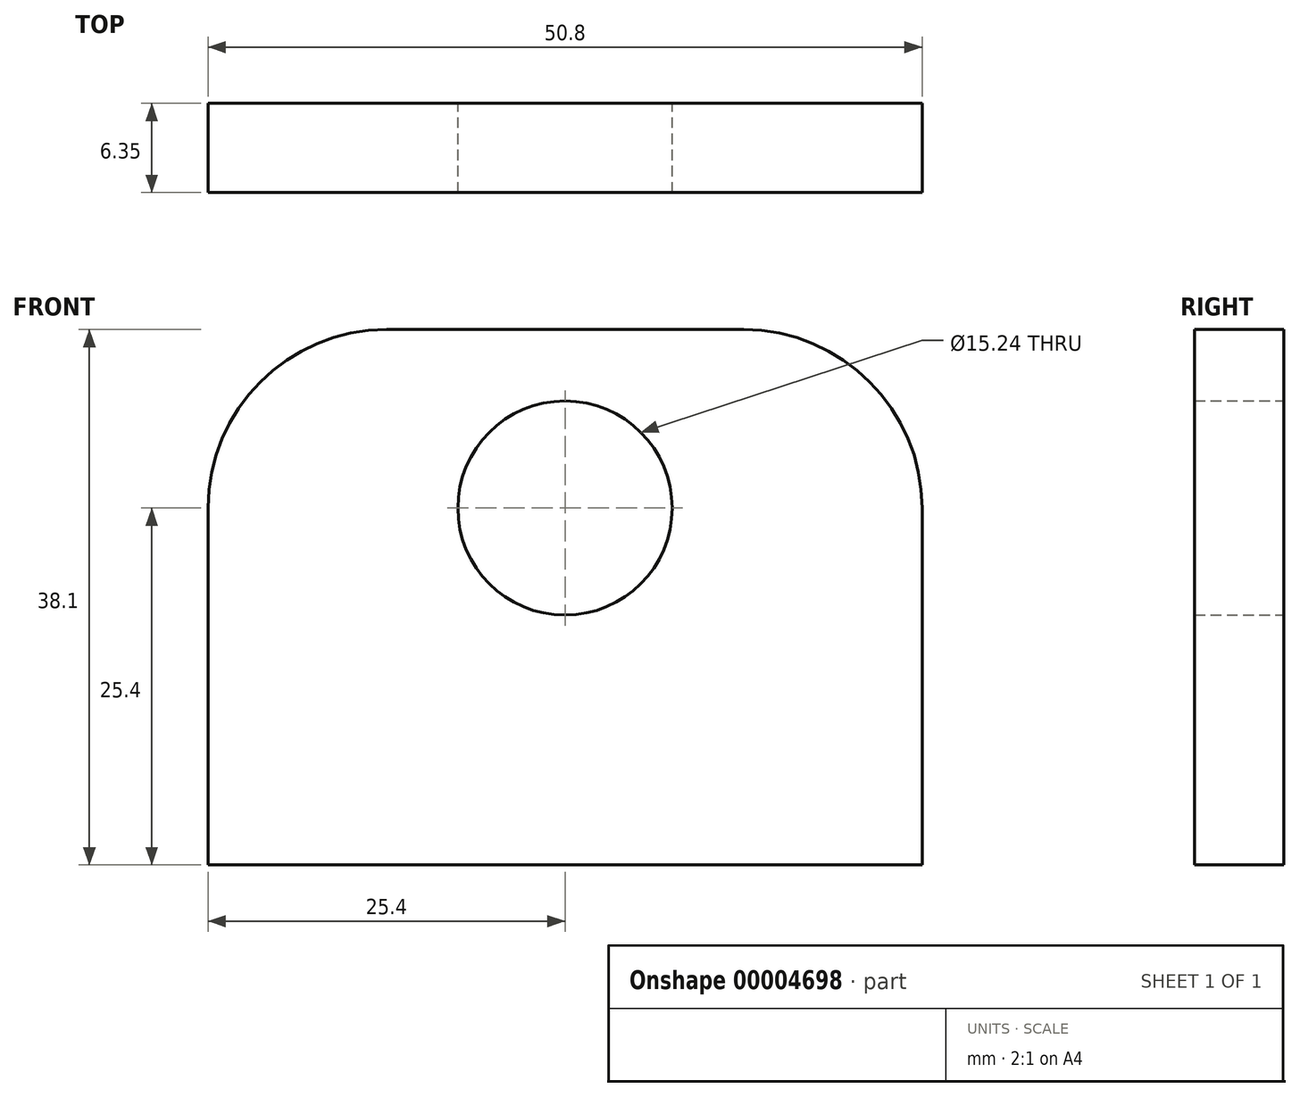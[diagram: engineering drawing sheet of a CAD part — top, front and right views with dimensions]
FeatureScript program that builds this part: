
annotation { "Feature Type Name" : "Feature", "Feature Type Description" : "" }
export const myFeature = defineFeature(function(context is Context, id is Id, definition is map)
    precondition{}
    {
        {
            var Q0;
            Q0=qCreatedBy(makeId("Front.planeOp"),FACE);
            var sketch = newSketch(context, id + "F0", { "sketchPlane" : qUnion([Q0])});
            skCircle(sketch, "E0", {"center": v(0, 0) * mm, "radius": 7.62 * mm});
            skLineSegment(sketch, "E1.rect.bottom", {"start": v(12.7, 12.7) * mm, "end": v(-12.7, 12.7) * mm});
            skLineSegment(sketch, "E1.rect.top", {"start": v(25.4, -25.4) * mm, "end": v(-25.4, -25.4) * mm});
            skLineSegment(sketch, "E1.rect.left", {"start": v(25.4, 0) * mm, "end": v(25.4, -25.4) * mm});
            skLineSegment(sketch, "E1.rect.right", {"start": v(-25.4, 0) * mm, "end": v(-25.4, -25.4) * mm});
            skPoint(sketch, "E1.rect.middle", {"position": v(0, -6.35) * mm});
            skPoint(sketch, "E2.visualSharp", {"position": v(-25.4, 12.7) * mm});
            skArc(sketch, "E2.filletArc", {"start": v(-12.7, 12.7) * mm, "mid": v(-21.68, 8.98) * mm, "end": v(-25.4, 0) * mm});
            skPoint(sketch, "E3.visualSharp", {"position": v(25.4, 12.7) * mm});
            skArc(sketch, "E3.filletArc", {"start": v(25.4, 0) * mm, "mid": v(21.68, 8.98) * mm, "end": v(12.7, 12.7) * mm});
            skSolve(sketch);
        }
        {
            var Q0;
            Q0 = qSketchRegion(id + "F0", true);
            extrude(context, id + "F1", {"entities" : qUnion([Q0]), "depth" : 6.35 * mm});
        }
    });
